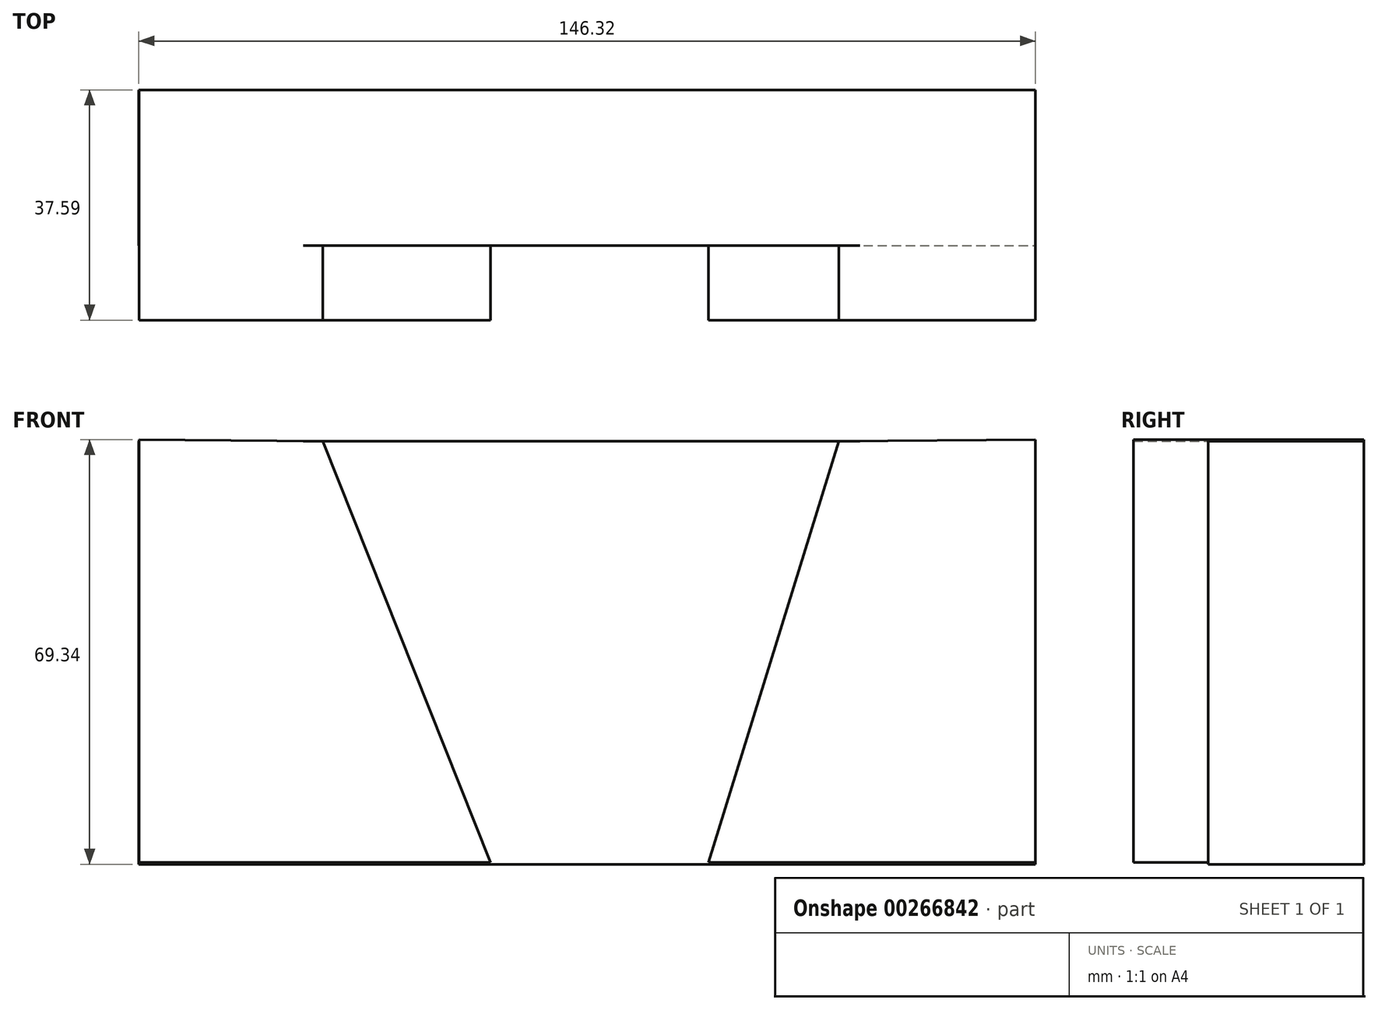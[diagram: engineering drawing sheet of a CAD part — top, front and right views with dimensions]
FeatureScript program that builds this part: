
annotation { "Feature Type Name" : "Feature", "Feature Type Description" : "" }
export const myFeature = defineFeature(function(context is Context, id is Id, definition is map)
    precondition{}
    {
        {
            var Q0;
            Q0=qCreatedBy(makeId("Front.planeOp"),FACE);
            var sketch = newSketch(context, id + "F0", { "sketchPlane" : qUnion([Q0])});
            skLineSegment(sketch, "E0.bottom", {"start": v(-73.16, 31.33) * mm, "end": v(73.16, 31.33) * mm});
            skLineSegment(sketch, "E0.top", {"start": v(-73.16, -37.75) * mm, "end": v(73.16, -37.75) * mm});
            skLineSegment(sketch, "E0.left", {"start": v(-73.16, 31.33) * mm, "end": v(-73.16, -37.75) * mm});
            skLineSegment(sketch, "E0.right", {"start": v(73.16, 31.33) * mm, "end": v(73.16, -37.75) * mm});
            skSolve(sketch);
        }
        {
            var Q0;
            Q0=qCreatedBy(makeId("Front.planeOp"),FACE);
            var sketch = newSketch(context, id + "F1", { "sketchPlane" : qUnion([Q0])});
            skLineSegment(sketch, "E1", {"start": v(-73.13, 31.6) * mm, "end": v(-73.13, -37.45) * mm});
            skLineSegment(sketch, "E2", {"start": v(-73.13, -37.45) * mm, "end": v(-15.73, -37.45) * mm});
            skLineSegment(sketch, "E3", {"start": v(-15.73, -37.45) * mm, "end": v(-43.12, 31.3) * mm});
            skLineSegment(sketch, "E4", {"start": v(-43.12, 31.3) * mm, "end": v(-73.13, 31.6) * mm});
            skLineSegment(sketch, "E5", {"start": v(73.12, 31.6) * mm, "end": v(73.12, -37.45) * mm});
            skLineSegment(sketch, "E6", {"start": v(73.12, -37.45) * mm, "end": v(19.81, -37.45) * mm});
            skLineSegment(sketch, "E7", {"start": v(19.81, -37.45) * mm, "end": v(41.08, 31.3) * mm});
            skLineSegment(sketch, "E8", {"start": v(41.08, 31.3) * mm, "end": v(73.12, 31.6) * mm});
            skSolve(sketch);
        }
        {
            var Q0;
            Q0 = qSketchRegion(id + "F0", true);
            extrude(context, id + "F2", {"entities" : qUnion([Q0]), "depth" : 25.4 * mm});
        }
        {
            var Q0;
            Q0 = qSketchRegion(id + "F1", true);
            extrude(context, id + "F3", {"entities" : qUnion([Q0]), "operationType" : NewBodyOperationType.ADD, "depth" : 37.6 * mm});
        }
    });
